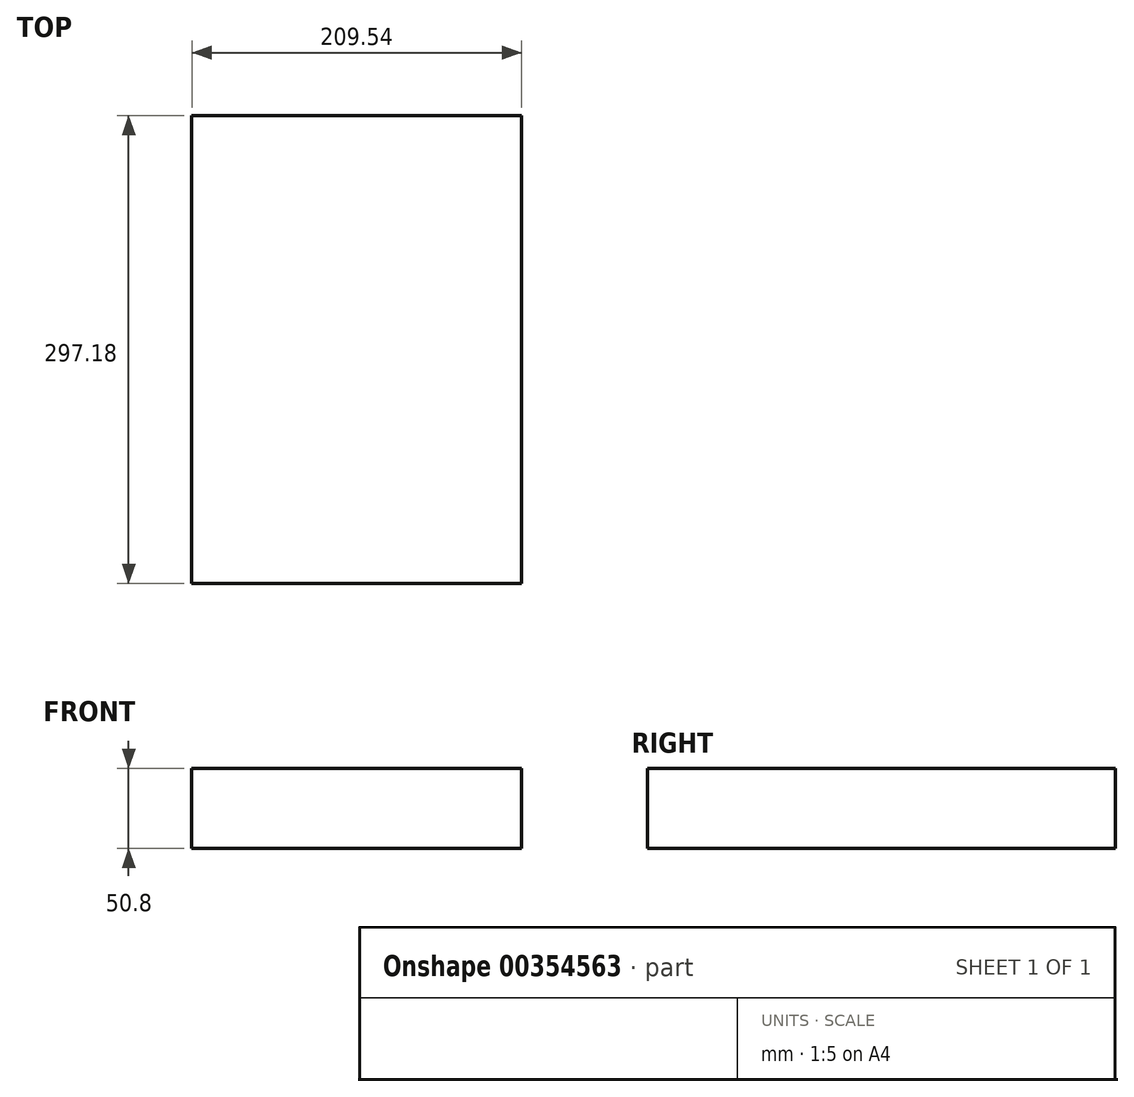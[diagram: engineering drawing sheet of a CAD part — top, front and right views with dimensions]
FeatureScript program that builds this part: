
annotation { "Feature Type Name" : "Feature", "Feature Type Description" : "" }
export const myFeature = defineFeature(function(context is Context, id is Id, definition is map)
    precondition{}
    {
        {
            var Q0;
            Q0=qCreatedBy(makeId("Top.planeOp"),FACE);
            var sketch = newSketch(context, id + "F0", { "sketchPlane" : qUnion([Q0])});
            skLineSegment(sketch, "E0.bottom", {"start": v(104.78, 148.6) * mm, "end": v(-104.77, 148.6) * mm});
            skLineSegment(sketch, "E0.top", {"start": v(104.77, -148.6) * mm, "end": v(-104.78, -148.6) * mm});
            skLineSegment(sketch, "E0.left", {"start": v(104.78, 148.6) * mm, "end": v(104.77, -148.6) * mm});
            skLineSegment(sketch, "E0.right", {"start": v(-104.77, 148.6) * mm, "end": v(-104.78, -148.6) * mm});
            skPoint(sketch, "E0.middle", {"position": v(0, 0) * mm});
            skSolve(sketch);
        }
        {
            var Q0;
            Q0=makeQuery(id+"F0.imprint","IMPRINT",FACE,{"disambiguationData":[TD([[makeQuery(id+"F0.imprint","IMPRINT",EDGE,{"derivedFrom":sQuery(id+"F0.wireOp",EDGE,"E0.bottom")}),1.0]])]});
            extrude(context, id + "F1", {"entities" : qUnion([Q0]), "depth" : 50.8 * mm});
        }
    });
